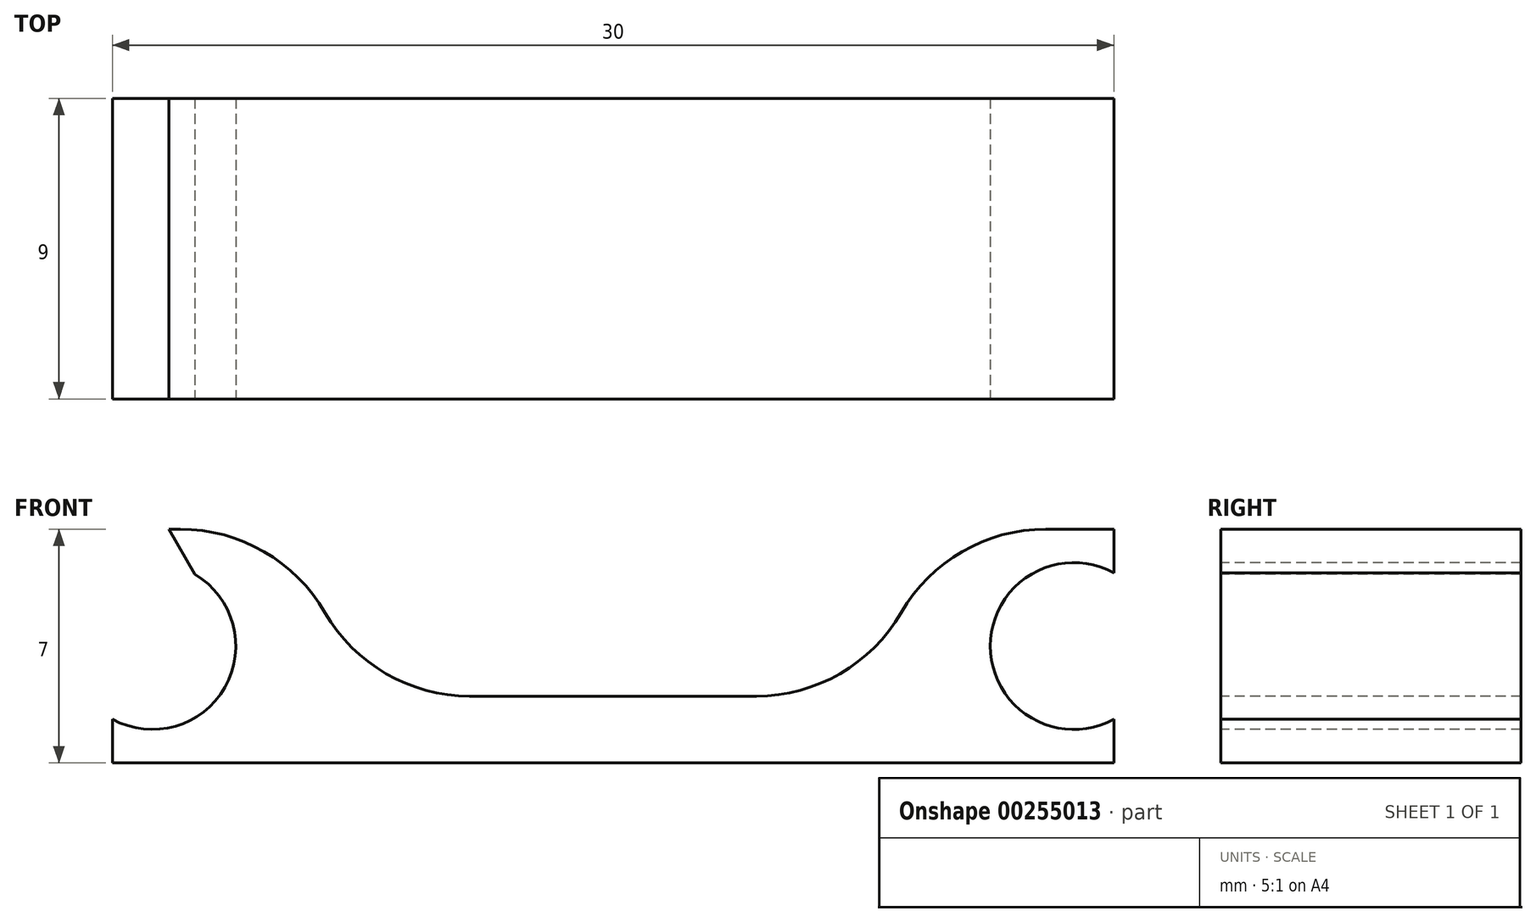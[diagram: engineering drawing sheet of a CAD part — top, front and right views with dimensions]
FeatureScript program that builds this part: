
annotation { "Feature Type Name" : "Feature", "Feature Type Description" : "" }
export const myFeature = defineFeature(function(context is Context, id is Id, definition is map)
    precondition{}
    {
        {
            var Q0;
            Q0=qCreatedBy(makeId("Top.planeOp"),FACE);
            var sketch = newSketch(context, id + "F0", { "sketchPlane" : qUnion([Q0])});
            skLineSegment(sketch, "E0.bottom", {"start": v(15, 4.5) * mm, "end": v(-15, 4.5) * mm});
            skLineSegment(sketch, "E0.top", {"start": v(15, -4.5) * mm, "end": v(-15, -4.5) * mm});
            skLineSegment(sketch, "E0.left", {"start": v(15, 4.5) * mm, "end": v(15, -4.5) * mm});
            skLineSegment(sketch, "E0.right", {"start": v(-15, 4.5) * mm, "end": v(-15, -4.5) * mm});
            skPoint(sketch, "E0.middle", {"position": v(0, 0) * mm});
            skSolve(sketch);
        }
        {
            var Q0;
            Q0=makeQuery(id+"F0.imprint","IMPRINT",FACE,{"disambiguationData":[TD([[makeQuery(id+"F0.imprint","IMPRINT",EDGE,{"derivedFrom":sQuery(id+"F0.wireOp",EDGE,"E0.bottom")}),1.0]])]});
            extrude(context, id + "F1", {"entities" : qUnion([Q0]), "depth" : 7 * mm});
        }
        {
            var Q0;
            Q0=makeQuery(id+"F1.opExtrude","SWEPT_FACE",FACE,{"disambiguationData":[OSD([sQuery(id+"F0.wireOp",EDGE,"E0.top")])]});
            var sketch = newSketch(context, id + "F2", { "sketchPlane" : qUnion([Q0])});
            skLineSegment(sketch, "E1", {"start": v(0, 0) * mm, "end": v(0, 7) * mm});
            skLineSegment(sketch, "E2", {"start": v(-15, 3.5) * mm, "end": v(15, 3.5) * mm});
            skCircle(sketch, "E3", {"center": v(-13.8, 3.5) * mm, "radius": 2.5 * mm});
            skCircle(sketch, "E4", {"center": v(13.8, 3.5) * mm, "radius": 2.5 * mm});
            skLineSegment(sketch, "E5", {"start": v(-13.8, 1) * mm, "end": v(13.8, 1) * mm});
            skPoint(sketch, "E6", {"position": v(0, 1) * mm});
            skSolve(sketch);
        }
        {
            var Q0;
            {var subQ0=sQuery(id+"F2.wireOp",EDGE,"E2");var subQ3=sQuery(id+"F2.wireOp",EDGE,"E3");var subQ4=makeQuery(id+"F2.imprint","INTERSECT",VERTEX,{"derivedFrom":[subQ0,subQ3]});Q0=makeQuery(id+"F2.imprint","IMPRINT",FACE,{"disambiguationData":[TD([[makeQuery(id+"F2.imprint","IMPRINT",EDGE,{"disambiguationData":[TD([[subQ4,1.0]])],"derivedFrom":subQ0}),1.0]])]});}
            var Q1;
            {var subQ0=sQuery(id+"F2.wireOp",EDGE,"E2");var subQ3=sQuery(id+"F2.wireOp",EDGE,"E4");var subQ4=makeQuery(id+"F2.imprint","INTERSECT",VERTEX,{"derivedFrom":[subQ0,subQ3]});Q1=makeQuery(id+"F2.imprint","IMPRINT",FACE,{"disambiguationData":[TD([[makeQuery(id+"F2.imprint","IMPRINT",EDGE,{"disambiguationData":[TD([[subQ4,-1.0]])],"derivedFrom":subQ0}),1.0]])]});}
            var Q2;
            {var subQ3=sQuery(id+"F2.wireOp",EDGE,"E4");var subQ5=makeQuery(id+"F2.imprint","INTERSECT",VERTEX,{"derivedFrom":[subQ3,sQuery(id+"F2.wireOp",EDGE,"E5")]});Q2=makeQuery(id+"F2.imprint","IMPRINT",FACE,{"disambiguationData":[TD([[makeQuery(id+"F2.imprint","IMPRINT",EDGE,{"disambiguationData":[TD([[subQ5,1.0]])],"derivedFrom":subQ3}),1.0]])]});}
            var Q3;
            {var subQ3=sQuery(id+"F2.wireOp",EDGE,"E3");var subQ5=makeQuery(id+"F2.imprint","INTERSECT",VERTEX,{"derivedFrom":[subQ3,sQuery(id+"F2.wireOp",EDGE,"E5")]});Q3=makeQuery(id+"F2.imprint","IMPRINT",FACE,{"disambiguationData":[TD([[makeQuery(id+"F2.imprint","IMPRINT",EDGE,{"disambiguationData":[TD([[subQ5,-1.0]])],"derivedFrom":subQ3}),1.0]])]});}
            extrude(context, id + "F3", {"entities" : qUnion([Q0, Q1, Q2, Q3]), "operationType" : NewBodyOperationType.REMOVE, "endBound" : BoundingType.THROUGH_ALL, "oppositeDirection" : true, "depth" : 25 * mm});
        }
        {
            var Q0;
            {var subQ0=sQuery(id+"F2.wireOp",EDGE,"E3");var subQ1=sQuery(id+"F0.wireOp",EDGE,"E0.right");var subQ2=sQuery(id+"F0.wireOp",EDGE,"E0.top");Q0=makeQuery(id+"F3.boolean.opBoolean","COPY",EDGE,{"derivedFrom":makeQuery(id+"F3.opExtrude","SWEPT_EDGE",EDGE,{"disambiguationData":[OSD([subQ2,subQ1,subQ0]),TDD([makeQuery(id+"F2.imprint","INTERSECT",VERTEX,{"disambiguationData":[OD(0.0)],"derivedFrom":[makeQuery(id+"F1.opExtrude","SWEPT_EDGE",EDGE,{"disambiguationData":[OSD([subQ2,subQ1])]}),subQ0]})])]})});}
            var Q1;
            {var subQ0=sQuery(id+"F2.wireOp",EDGE,"E4");var subQ1=sQuery(id+"F0.wireOp",EDGE,"E0.left");var subQ2=sQuery(id+"F0.wireOp",EDGE,"E0.top");Q1=makeQuery(id+"F3.boolean.opBoolean","COPY",EDGE,{"derivedFrom":makeQuery(id+"F3.opExtrude","SWEPT_EDGE",EDGE,{"disambiguationData":[OSD([subQ2,subQ1,subQ0]),TDD([makeQuery(id+"F2.imprint","INTERSECT",VERTEX,{"disambiguationData":[OD(0.0)],"derivedFrom":[makeQuery(id+"F1.opExtrude","SWEPT_EDGE",EDGE,{"disambiguationData":[OSD([subQ2,subQ1])]}),subQ0]})])]})});}
            chamfer(context, id + "F4", {"entities" : qUnion([Q0, Q1]), "width" : 5 * mm, "tangentPropagation" : true});
        }
        {
            var Q0;
            Q0=makeQuery(id+"F1.opExtrude","SWEPT_FACE",FACE,{"disambiguationData":[OSD([sQuery(id+"F0.wireOp",EDGE,"E0.top")])]});
            var sketch = newSketch(context, id + "F5", { "sketchPlane" : qUnion([Q0])});
            skLineSegment(sketch, "E7.bottom", {"start": v(-9.3, 7) * mm, "end": v(9.3, 7) * mm});
            skLineSegment(sketch, "E7.top", {"start": v(-9.3, 2) * mm, "end": v(9.3, 2) * mm});
            skLineSegment(sketch, "E7.left", {"start": v(-9.3, 7) * mm, "end": v(-9.3, 2) * mm});
            skLineSegment(sketch, "E7.right", {"start": v(9.3, 7) * mm, "end": v(9.3, 2) * mm});
            skSolve(sketch);
        }
        {
            var Q0;
            Q0=makeQuery(id+"F5.imprint","IMPRINT",FACE,{"disambiguationData":[TD([[makeQuery(id+"F5.imprint","IMPRINT",EDGE,{"derivedFrom":sQuery(id+"F5.wireOp",EDGE,"E7.bottom")}),1.0]])]});
            extrude(context, id + "F6", {"entities" : qUnion([Q0]), "operationType" : NewBodyOperationType.REMOVE, "endBound" : BoundingType.THROUGH_ALL, "oppositeDirection" : true, "depth" : 25 * mm});
        }
        {
            var Q0;
            Q0=makeQuery(id+"F6.boolean.opBoolean","COPY",EDGE,{"derivedFrom":makeQuery(id+"F6.opExtrude","SWEPT_EDGE",EDGE,{"disambiguationData":[OSD([sQuery(id+"F5.wireOp",EDGE,"E7.top"),sQuery(id+"F5.wireOp",EDGE,"E7.right")])]})});
            var Q1;
            Q1=makeQuery(id+"F6.boolean.opBoolean","COPY",EDGE,{"derivedFrom":makeQuery(id+"F6.opExtrude","SWEPT_EDGE",EDGE,{"disambiguationData":[OSD([sQuery(id+"F5.wireOp",EDGE,"E7.top"),sQuery(id+"F5.wireOp",EDGE,"E7.left")])]})});
            fillet(context, id + "F7", {"entities" : qUnion([Q0, Q1]), "radius" : 5 * mm, "tangentPropagation" : true, "allowEdgeOverflow" : false});
        }
        {
            var Q0;
            {var subQ0=sQuery(id+"F0.wireOp",EDGE,"E0.bottom");var subQ1=sQuery(id+"F0.wireOp",EDGE,"E0.right");var subQ2=sQuery(id+"F0.wireOp",EDGE,"E0.top");var subQ3=sQuery(id+"F5.wireOp",EDGE,"E7.left");Q0=makeQuery(id+"F7.opFillet","BLEND_EDGE",EDGE,{"blendedFrom":[makeQuery(id+"F6.boolean.opBoolean","COPY",EDGE,{"derivedFrom":makeQuery(id+"F6.opExtrude","SWEPT_EDGE",EDGE,{"disambiguationData":[OSD([sQuery(id+"F5.wireOp",EDGE,"E7.top"),subQ3])]})}),makeQuery(id+"F6.boolean.opBoolean","SPLIT",FACE,{"disambiguationData":[TD([makeQuery(id+"F6.opExtrude","SWEPT_FACE",FACE,{"disambiguationData":[OSD([subQ3])]})])],"derivedFrom":makeQuery(id+"F1.opExtrude","CAP_FACE",FACE,{"disambiguationData":[OSD([subQ0,subQ2,sQuery(id+"F0.wireOp",EDGE,"E0.left"),subQ1])],"isStart":false})})],"blendedInto":[makeQuery(id+"F6.boolean.opBoolean","SPLIT",FACE,{"disambiguationData":[TD([makeQuery(id+"F6.opExtrude","SWEPT_FACE",FACE,{"disambiguationData":[OSD([subQ3])]})])],"derivedFrom":makeQuery(id+"F1.opExtrude","CAP_FACE",FACE,{"disambiguationData":[OSD([subQ0,subQ2,sQuery(id+"F0.wireOp",EDGE,"E0.left"),subQ1])],"isStart":false})})]});}
            var Q1;
            {var subQ0=sQuery(id+"F0.wireOp",EDGE,"E0.bottom");var subQ1=sQuery(id+"F0.wireOp",EDGE,"E0.top");var subQ2=sQuery(id+"F0.wireOp",EDGE,"E0.left");var subQ3=sQuery(id+"F5.wireOp",EDGE,"E7.right");Q1=makeQuery(id+"F7.opFillet","BLEND_EDGE",EDGE,{"blendedFrom":[makeQuery(id+"F6.boolean.opBoolean","COPY",EDGE,{"derivedFrom":makeQuery(id+"F6.opExtrude","SWEPT_EDGE",EDGE,{"disambiguationData":[OSD([sQuery(id+"F5.wireOp",EDGE,"E7.top"),subQ3])]})}),makeQuery(id+"F6.boolean.opBoolean","SPLIT",FACE,{"disambiguationData":[TD([makeQuery(id+"F6.opExtrude","SWEPT_FACE",FACE,{"disambiguationData":[OSD([subQ3])]})])],"derivedFrom":makeQuery(id+"F1.opExtrude","CAP_FACE",FACE,{"disambiguationData":[OSD([subQ0,subQ1,subQ2,sQuery(id+"F0.wireOp",EDGE,"E0.right")])],"isStart":false})})],"blendedInto":[makeQuery(id+"F6.boolean.opBoolean","SPLIT",FACE,{"disambiguationData":[TD([makeQuery(id+"F6.opExtrude","SWEPT_FACE",FACE,{"disambiguationData":[OSD([subQ3])]})])],"derivedFrom":makeQuery(id+"F1.opExtrude","CAP_FACE",FACE,{"disambiguationData":[OSD([subQ0,subQ1,subQ2,sQuery(id+"F0.wireOp",EDGE,"E0.right")])],"isStart":false})})]});}
            fillet(context, id + "F8", {"entities" : qUnion([Q0, Q1]), "radius" : 5 * mm, "tangentPropagation" : true, "allowEdgeOverflow" : false});
        }
    });
